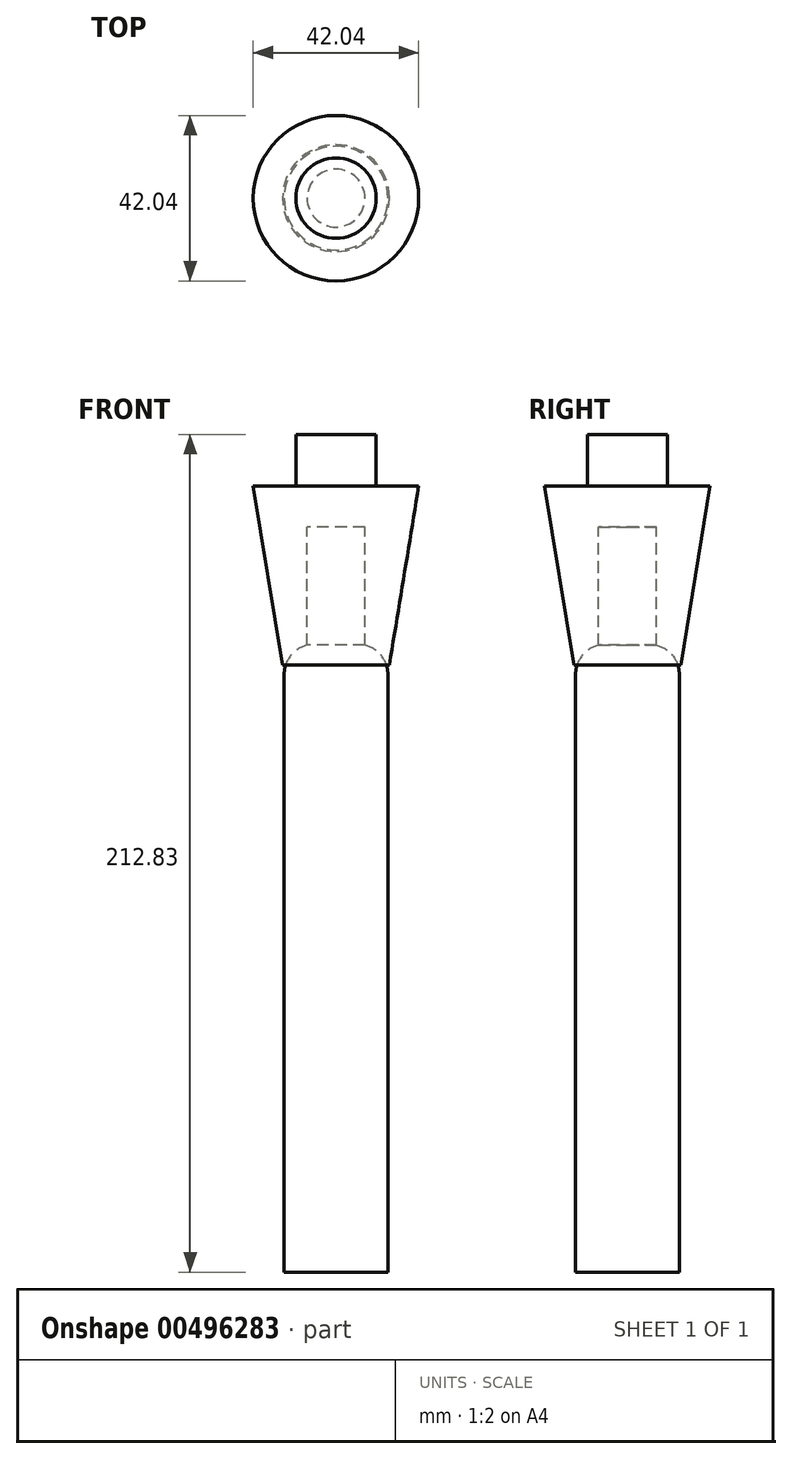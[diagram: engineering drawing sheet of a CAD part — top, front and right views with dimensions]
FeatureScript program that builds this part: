
annotation { "Feature Type Name" : "Feature", "Feature Type Description" : "" }
export const myFeature = defineFeature(function(context is Context, id is Id, definition is map)
    precondition{}
    {
        {
            var Q0;
            Q0=qCreatedBy(makeId("Front.planeOp"),FACE);
            var sketch = newSketch(context, id + "F0", { "sketchPlane" : qUnion([Q0])});
            skLineSegment(sketch, "E0", {"start": v(0, 0) * mm, "end": v(13.18, 0) * mm});
            skLineSegment(sketch, "E1", {"start": v(13.18, 0) * mm, "end": v(13.18, 151.86) * mm});
            skLineSegment(sketch, "E2", {"start": v(7.35, 159.26) * mm, "end": v(7.35, 189.3) * mm});
            skLineSegment(sketch, "E3", {"start": v(7.35, 189.3) * mm, "end": v(0, 189.3) * mm});
            skLineSegment(sketch, "E4", {"start": v(0, 189.3) * mm, "end": v(0, 0) * mm});
            skArc(sketch, "E5", {"start": v(13.18, 151.86) * mm, "mid": v(11.55, 156.57) * mm, "end": v(7.35, 159.26) * mm});
            skSolve(sketch);
        }
        {
            var Q0;
            Q0 = qSketchRegion(id + "F0", true);
            var Q1;
            Q1=sQuery(id+"F0.wireOp",EDGE,"E4");
            revolve(context, id + "F1", {"entities" : qUnion([Q0]), "axis" : qUnion([Q1]), "revolveType" : RevolveType.FULL});
        }
        {
            var Q0;
            Q0=qCreatedBy(makeId("Front.planeOp"),FACE);
            var sketch = newSketch(context, id + "F2", { "sketchPlane" : qUnion([Q0])});
            skLineSegment(sketch, "E6.0", {"start": v(-13.18, 151.86) * mm, "end": v(13.18, 151.86) * mm});
            skLineSegment(sketch, "E7", {"start": v(13.57, 154.28) * mm, "end": v(21.02, 199.73) * mm});
            skLineSegment(sketch, "E8", {"start": v(21.02, 199.73) * mm, "end": v(10.2, 199.73) * mm});
            skLineSegment(sketch, "E9", {"start": v(10.2, 199.73) * mm, "end": v(10.2, 212.83) * mm});
            skLineSegment(sketch, "E10", {"start": v(10.2, 212.83) * mm, "end": v(0, 212.83) * mm});
            skLineSegment(sketch, "E11", {"start": v(0, 212.83) * mm, "end": v(0, 154.28) * mm});
            skLineSegment(sketch, "E12", {"start": v(0, 154.28) * mm, "end": v(13.57, 154.28) * mm});
            skSolve(sketch);
        }
        {
            var Q0;
            Q0 = qSketchRegion(id + "F2", true);
            var Q1;
            Q1=sQuery(id+"F2.wireOp",EDGE,"E11");
            revolve(context, id + "F3", {"entities" : qUnion([Q0]), "axis" : qUnion([Q1]), "revolveType" : RevolveType.FULL});
        }
    });
